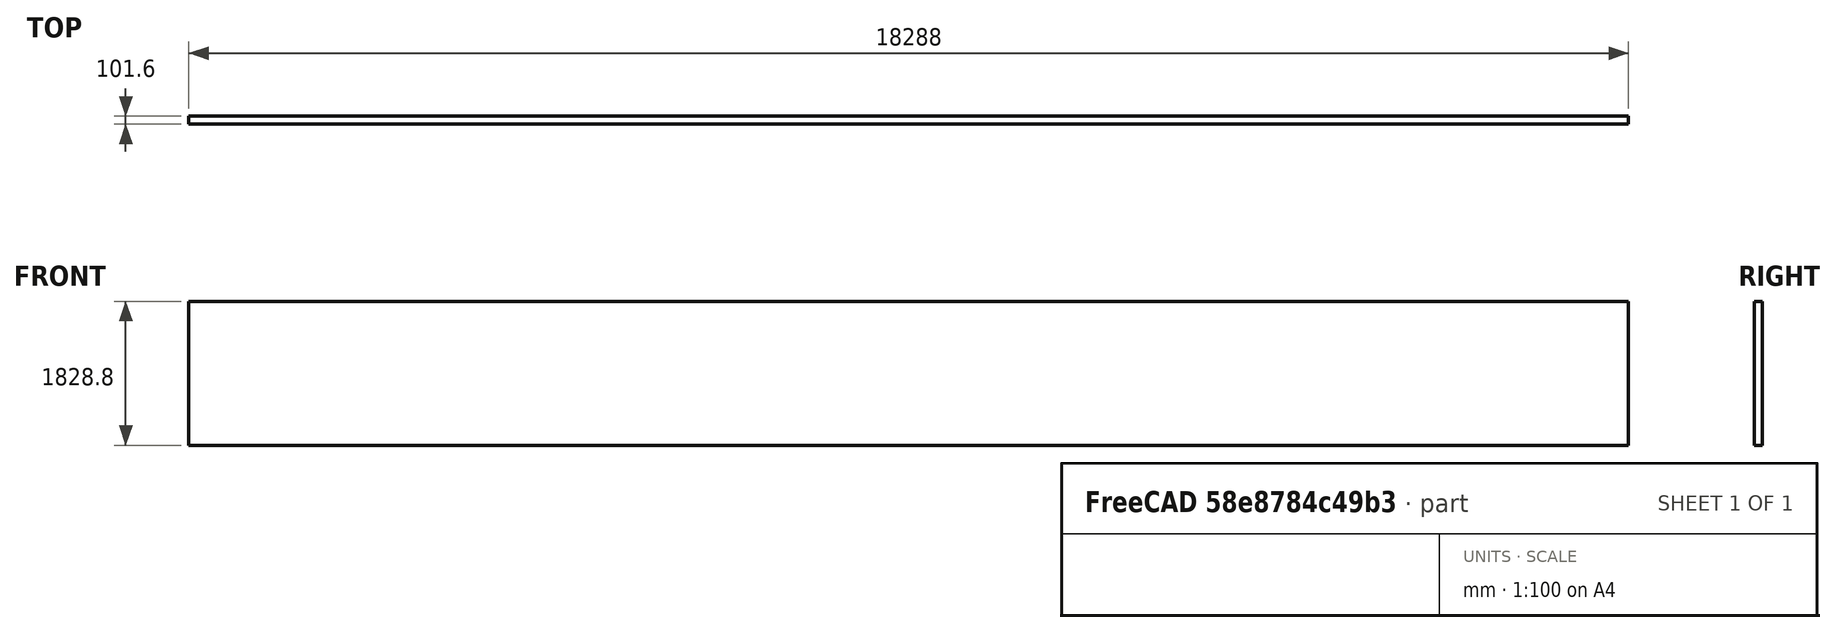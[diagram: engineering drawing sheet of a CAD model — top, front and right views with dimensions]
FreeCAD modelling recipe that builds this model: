
FCSTD DOCUMENT  (FreeCAD 0.20R29177 (Git))
Label: backfence
License: All rights reserved
LicenseURL: http://en.wikipedia.org/wiki/All_rights_reserved
objects: Sketcher::SketchObject×1, PartDesign::Pad×1, PartDesign::Body×1
note: 4 computed .brp shape members not serialized (recipe doc carries the construction recipe); baked Part::Feature solids carry a one-line shape summary decoded from their .brp

FEATURE [Sketcher::SketchObject] Sketch
  FullyConstrained = true
  MapMode = 5
  Placement = pos=(0,0,0) rot=(1,0,0;1.5708rad)
  Support = -> [XZ_Plane]
  expr: Constraints[10] = 60 * 12 * 25.4
  expr: Constraints[9] = 6 * 12 * 25.4
  sketch-geometry (4):
    g0: LineSegment StartX=0 StartY=0 StartZ=0 EndX=-18288 EndY=0 EndZ=0
    g1: LineSegment StartX=-18288 StartY=0 StartZ=0 EndX=-18288 EndY=1828.8 EndZ=0
    g2: LineSegment StartX=-18288 StartY=1828.8 StartZ=0 EndX=0 EndY=1828.8 EndZ=0
    g3: LineSegment StartX=0 StartY=1828.8 StartZ=0 EndX=0 EndY=0 EndZ=0
  constraints (11):
    c: Coincident(g0,g1)
    c: Coincident(g1,g2)
    c: Coincident(g2,g3)
    c: Coincident(g3,g0)
    c: Horizontal(g0)
    c: Horizontal(g2)
    c: Vertical(g1)
    c: Vertical(g3)
    c: Coincident(g0,g-1)
    c: DistanceY(g3,g3) = 1828.8
    c: DistanceX(g0,g0) = 18288
FEATURE [PartDesign::Pad] Pad
  Direction = (0,-1,2e-16)
  Length = 101.6
  Length2 = 10
  Placement = pos=(0,0,0) rot=(1,0,0;1.5708rad)
  Profile = -> Sketch
  ReferenceAxis = -> Sketch [N_Axis]
  Type = 0
  expr: Length = 4 * 25.4
FEATURE [PartDesign::Body] Body
  Group = -> [Sketch,Pad]
  Origin = -> Origin
  Tip = -> Pad
